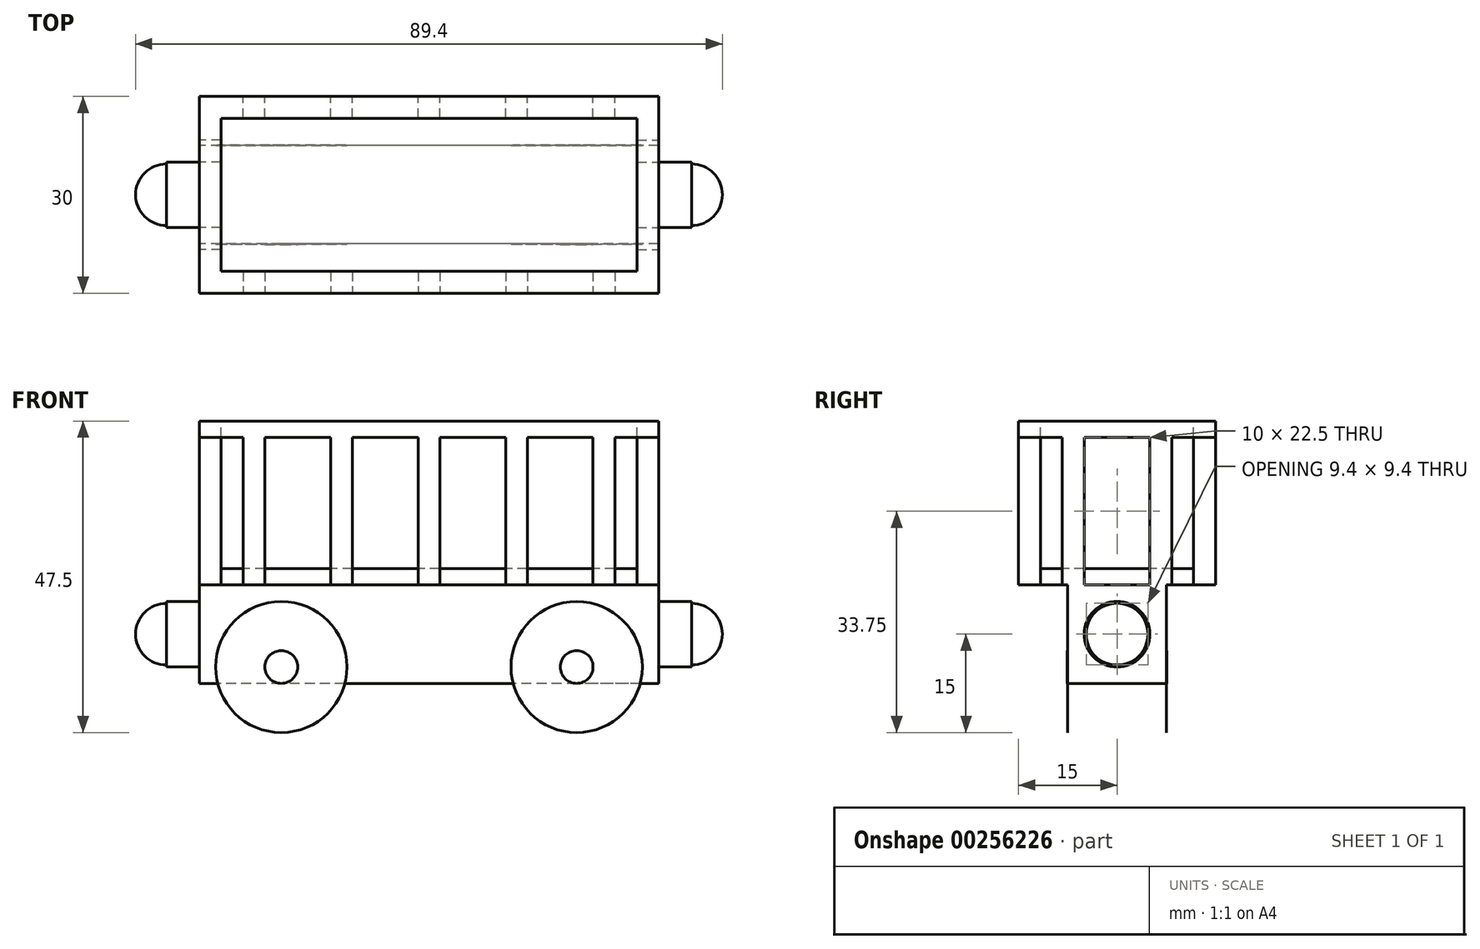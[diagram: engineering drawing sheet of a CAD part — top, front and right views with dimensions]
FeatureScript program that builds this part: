
annotation { "Feature Type Name" : "Feature", "Feature Type Description" : "" }
export const myFeature = defineFeature(function(context is Context, id is Id, definition is map)
    precondition{}
    {
        {
            var Q0;
            Q0=qCreatedBy(makeId("Front.planeOp"),FACE);
            var sketch = newSketch(context, id + "F0", { "sketchPlane" : qUnion([Q0])});
            skLineSegment(sketch, "E0.bottom", {"start": v(35, 7.5) * mm, "end": v(-35, 7.5) * mm});
            skLineSegment(sketch, "E0.top", {"start": v(35, -7.5) * mm, "end": v(-35, -7.5) * mm});
            skLineSegment(sketch, "E0.left", {"start": v(35, 7.5) * mm, "end": v(35, -7.5) * mm});
            skLineSegment(sketch, "E0.right", {"start": v(-35, 7.5) * mm, "end": v(-35, -7.5) * mm});
            skPoint(sketch, "E0.middle", {"position": v(0, 0) * mm});
            skSolve(sketch);
        }
        {
            var Q0;
            Q0=makeQuery(id+"F0.imprint","IMPRINT",FACE,{"disambiguationData":[TD([[makeQuery(id+"F0.imprint","IMPRINT",EDGE,{"derivedFrom":sQuery(id+"F0.wireOp",EDGE,"E0.bottom")}),1.0]])]});
            extrude(context, id + "F1", {"entities" : qUnion([Q0]), "flatOperationType" : FlatOperationType.REMOVE, "endBound" : BoundingType.SYMMETRIC, "offsetDistance" : 25.4 * mm, "depth" : 15 * mm, "domain" : OperationDomain.MODEL});
        }
        {
            var Q0;
            Q0=makeQuery(id+"F1.opExtrude","SWEPT_FACE",FACE,{"disambiguationData":[OSD([sQuery(id+"F0.wireOp",EDGE,"E0.left")])]});
            var sketch = newSketch(context, id + "F2", { "sketchPlane" : qUnion([Q0])});
            skCircle(sketch, "E1", {"center": v(0, 0) * mm, "radius": 5 * mm});
            skSolve(sketch);
        }
        {
            var Q0;
            Q0 = qSketchRegion(id + "F2", true);
            var Q1;
            Q1 = qSketchRegion(id + "F4", true);
            extrude(context, id + "F3", {"entities" : qUnion([Q0, Q1]), "operationType" : NewBodyOperationType.ADD, "flatOperationType" : FlatOperationType.REMOVE, "offsetDistance" : 25.4 * mm, "depth" : 5 * mm, "domain" : OperationDomain.MODEL});
        }
        {
            var Q0;
            Q0=makeQuery(id+"F3.opExtrude","CAP_FACE",FACE,{"disambiguationData":[OSD([sQuery(id+"F2.wireOp",EDGE,"E1")])],"isStart":false});
            var sketch = newSketch(context, id + "F4", { "sketchPlane" : qUnion([Q0])});
            skArc(sketch, "E2", {"start": v(0, -4.7) * mm, "mid": v(4.7, 0) * mm, "end": v(0, 4.7) * mm});
            skLineSegment(sketch, "E3", {"start": v(0, 4.7) * mm, "end": v(0, -4.7) * mm});
            skSolve(sketch);
        }
        {
            var Q0;
            Q0 = qSketchRegion(id + "F4", true);
            var Q1;
            Q1=sQuery(id+"F4.wireOp",EDGE,"E3");
            revolve(context, id + "F5", {"operationType" : NewBodyOperationType.ADD, "surfaceOperationType" : NewSurfaceOperationType.NEW, "entities" : qUnion([Q0]), "axis" : qUnion([Q1]), "revolveType" : RevolveType.FULL});
        }
        {
            var Q0;
            Q0=makeQuery(id+"F1.opExtrude","SWEPT_FACE",FACE,{"disambiguationData":[OSD([sQuery(id+"F0.wireOp",EDGE,"E0.right")])]});
            var sketch = newSketch(context, id + "F6", { "sketchPlane" : qUnion([Q0])});
            skCircle(sketch, "E4", {"center": v(0, 0) * mm, "radius": 5 * mm});
            skSolve(sketch);
        }
        {
            var Q0;
            Q0 = qSketchRegion(id + "F6", true);
            extrude(context, id + "F7", {"entities" : qUnion([Q0]), "operationType" : NewBodyOperationType.ADD, "depth" : 5 * mm});
        }
        {
            var Q0;
            Q0=makeQuery(id+"F7.opExtrude","CAP_FACE",FACE,{"disambiguationData":[OSD([sQuery(id+"F6.wireOp",EDGE,"E4")])],"isStart":false});
            var sketch = newSketch(context, id + "F8", { "sketchPlane" : qUnion([Q0])});
            skArc(sketch, "E5", {"start": v(0, -4.7) * mm, "mid": v(4.7, 0) * mm, "end": v(0, 4.7) * mm});
            skLineSegment(sketch, "E6", {"start": v(0, 4.7) * mm, "end": v(0, -4.7) * mm});
            skSolve(sketch);
        }
        {
            var Q0;
            Q0=makeQuery(id+"F8.imprint","IMPRINT",FACE,{"disambiguationData":[TD([[makeQuery(id+"F8.imprint","IMPRINT",EDGE,{"derivedFrom":sQuery(id+"F8.wireOp",EDGE,"E5")}),1.0]])]});
            var Q1;
            Q1=sQuery(id+"F8.wireOp",EDGE,"E6");
            revolve(context, id + "F9", {"operationType" : NewBodyOperationType.ADD, "entities" : qUnion([Q0]), "axis" : qUnion([Q1]), "revolveType" : RevolveType.FULL});
        }
        {
            var Q0;
            Q0=makeQuery(id+"F1.opExtrude","SWEPT_FACE",FACE,{"disambiguationData":[OSD([sQuery(id+"F0.wireOp",EDGE,"E0.bottom")])]});
            var sketch = newSketch(context, id + "F10", { "sketchPlane" : qUnion([Q0])});
            skLineSegment(sketch, "E7.bottom", {"start": v(35, 15) * mm, "end": v(-35, 15) * mm});
            skLineSegment(sketch, "E7.top", {"start": v(35, -15) * mm, "end": v(-35, -15) * mm});
            skLineSegment(sketch, "E7.left", {"start": v(35, 15) * mm, "end": v(35, -15) * mm});
            skLineSegment(sketch, "E7.right", {"start": v(-35, 15) * mm, "end": v(-35, -15) * mm});
            skPoint(sketch, "E7.middle", {"position": v(0, 0) * mm});
            skSolve(sketch);
        }
        {
            var Q0;
            Q0 = qSketchRegion(id + "F10", true);
            extrude(context, id + "F11", {"entities" : qUnion([Q0]), "operationType" : NewBodyOperationType.ADD, "flatOperationType" : FlatOperationType.REMOVE, "offsetDistance" : 25.4 * mm, "depth" : 25 * mm, "domain" : OperationDomain.MODEL});
        }
        {
            var Q0;
            Q0=makeQuery(id+"F11.opExtrude","CAP_FACE",FACE,{"disambiguationData":[OSD([sQuery(id+"F10.wireOp",EDGE,"E7.bottom"),sQuery(id+"F10.wireOp",EDGE,"E7.top"),sQuery(id+"F10.wireOp",EDGE,"E7.left"),sQuery(id+"F10.wireOp",EDGE,"E7.right")])],"isStart":false});
            var sketch = newSketch(context, id + "F12", { "sketchPlane" : qUnion([Q0])});
            skLineSegment(sketch, "E8.bottom", {"start": v(31.67, 11.67) * mm, "end": v(-31.67, 11.67) * mm});
            skLineSegment(sketch, "E8.top", {"start": v(31.67, -11.67) * mm, "end": v(-31.67, -11.67) * mm});
            skLineSegment(sketch, "E8.left", {"start": v(31.67, 11.67) * mm, "end": v(31.67, -11.67) * mm});
            skLineSegment(sketch, "E8.right", {"start": v(-31.67, 11.67) * mm, "end": v(-31.67, -11.67) * mm});
            skPoint(sketch, "E8.middle", {"position": v(0, 0) * mm});
            skSolve(sketch);
        }
        {
            var Q0;
            Q0 = qSketchRegion(id + "F12", true);
            extrude(context, id + "F13", {"entities" : qUnion([Q0]), "operationType" : NewBodyOperationType.REMOVE, "flatOperationType" : FlatOperationType.REMOVE, "oppositeDirection" : true, "offsetDistance" : 25.4 * mm, "depth" : 22.5 * mm, "domain" : OperationDomain.MODEL});
        }
        {
            var Q0;
            Q0=makeQuery(id+"F11.opExtrude","SWEPT_FACE",FACE,{"disambiguationData":[OSD([sQuery(id+"F10.wireOp",EDGE,"E7.top")])]});
            var sketch = newSketch(context, id + "F14", { "sketchPlane" : qUnion([Q0])});
            skLineSegment(sketch, "E9", {"start": v(0, 39.89) * mm, "end": v(0, -16.72) * mm, "construction": true});
            skLineSegment(sketch, "E10.bottom", {"start": v(11.67, 30) * mm, "end": v(1.67, 30) * mm});
            skLineSegment(sketch, "E10.top", {"start": v(11.67, 7.5) * mm, "end": v(1.67, 7.5) * mm});
            skLineSegment(sketch, "E10.left", {"start": v(11.67, 30) * mm, "end": v(11.67, 7.5) * mm});
            skLineSegment(sketch, "E10.right", {"start": v(1.67, 30) * mm, "end": v(1.67, 7.5) * mm});
            skPoint(sketch, "E10.middle", {"position": v(6.67, 18.75) * mm});
            skSolve(sketch);
        }
        {
            var Q0;
            Q0=makeQuery(id+"F14.imprint","IMPRINT",FACE,{"disambiguationData":[TD([[makeQuery(id+"F14.imprint","IMPRINT",EDGE,{"derivedFrom":sQuery(id+"F14.wireOp",EDGE,"E10.bottom")}),1.0]])]});
            extrude(context, id + "F15", {"entities" : qUnion([Q0]), "operationType" : NewBodyOperationType.REMOVE, "flatOperationType" : FlatOperationType.REMOVE, "oppositeDirection" : true, "offsetDistance" : 25.4 * mm, "depth" : 5 * mm, "domain" : OperationDomain.MODEL});
        }
        {
            var Q0;
            Q0=makeQuery(id+"F11.opExtrude","SWEPT_FACE",FACE,{"disambiguationData":[OSD([sQuery(id+"F10.wireOp",EDGE,"E7.bottom")])]});
            var sketch = newSketch(context, id + "F16", { "sketchPlane" : qUnion([Q0])});
            skLineSegment(sketch, "E11.0", {"start": v(-11.67, 30) * mm, "end": v(-11.67, 10) * mm});
            skPoint(sketch, "E12.0", {"position": v(-6.67, 30) * mm});
            skLineSegment(sketch, "E13.0", {"start": v(-11.67, 30) * mm, "end": v(-1.67, 30) * mm});
            skLineSegment(sketch, "E14.0", {"start": v(-1.67, 30) * mm, "end": v(-1.67, 10) * mm});
            skLineSegment(sketch, "E15.0", {"start": v(-11.67, 10) * mm, "end": v(-11.67, 7.5) * mm});
            skPoint(sketch, "E16.0", {"position": v(-1.67, 8.75) * mm});
            skPoint(sketch, "E17.0", {"position": v(-1.67, 7.5) * mm});
            skLineSegment(sketch, "E18.0", {"start": v(-1.67, 10) * mm, "end": v(-1.67, 7.5) * mm});
            skLineSegment(sketch, "E19.top", {"start": v(-11.67, 7.5) * mm, "end": v(-1.67, 7.5) * mm});
            skLineSegment(sketch, "E19.left", {"start": v(-11.67, 30) * mm, "end": v(-11.67, 7.5) * mm});
            skLineSegment(sketch, "E19.right", {"start": v(-1.67, 30) * mm, "end": v(-1.67, 7.5) * mm});
            skSolve(sketch);
        }
        {
            var Q0;
            Q0 = qSketchRegion(id + "F16", true);
            extrude(context, id + "F17", {"entities" : qUnion([Q0]), "operationType" : NewBodyOperationType.REMOVE, "flatOperationType" : FlatOperationType.REMOVE, "oppositeDirection" : true, "offsetDistance" : 25.4 * mm, "depth" : 5 * mm, "domain" : OperationDomain.MODEL});
        }
        {
            var Q0;
            Q0=makeQuery(id+"F11.opExtrude","SWEPT_FACE",FACE,{"disambiguationData":[OSD([sQuery(id+"F10.wireOp",EDGE,"E7.top")])]});
            var sketch = newSketch(context, id + "F18", { "sketchPlane" : qUnion([Q0])});
            skLineSegment(sketch, "E20.bottom", {"start": v(25, 30) * mm, "end": v(15, 30) * mm});
            skLineSegment(sketch, "E20.top", {"start": v(25, 7.5) * mm, "end": v(15, 7.5) * mm});
            skLineSegment(sketch, "E20.left", {"start": v(25, 30) * mm, "end": v(25, 7.5) * mm});
            skLineSegment(sketch, "E20.right", {"start": v(15, 30) * mm, "end": v(15, 7.5) * mm});
            skPoint(sketch, "E20.middle", {"position": v(20, 18.75) * mm});
            skSolve(sketch);
        }
        {
            var Q0;
            Q0=makeQuery(id+"F18.imprint","IMPRINT",FACE,{"disambiguationData":[TD([[makeQuery(id+"F18.imprint","IMPRINT",EDGE,{"derivedFrom":sQuery(id+"F18.wireOp",EDGE,"E20.bottom")}),1.0]])]});
            extrude(context, id + "F19", {"entities" : qUnion([Q0]), "operationType" : NewBodyOperationType.REMOVE, "oppositeDirection" : true, "depth" : 5 * mm});
        }
        {
            var Q0;
            Q0=makeQuery(id+"F11.opExtrude","SWEPT_FACE",FACE,{"disambiguationData":[OSD([sQuery(id+"F10.wireOp",EDGE,"E7.bottom")])]});
            var sketch = newSketch(context, id + "F20", { "sketchPlane" : qUnion([Q0])});
            skLineSegment(sketch, "E21.0", {"start": v(-25, 30) * mm, "end": v(-25, 10) * mm});
            skLineSegment(sketch, "E22.0", {"start": v(-25, 30) * mm, "end": v(-15, 30) * mm});
            skLineSegment(sketch, "E23.0", {"start": v(-15, 30) * mm, "end": v(-15, 10) * mm});
            skLineSegment(sketch, "E24.0", {"start": v(-25, 10) * mm, "end": v(-25, 7.5) * mm});
            skLineSegment(sketch, "E25.0", {"start": v(-15, 10) * mm, "end": v(-15, 7.5) * mm});
            skLineSegment(sketch, "E26", {"start": v(-25, 7.5) * mm, "end": v(-15, 7.5) * mm});
            skSolve(sketch);
        }
        {
            var Q0;
            Q0 = qSketchRegion(id + "F20", true);
            extrude(context, id + "F21", {"entities" : qUnion([Q0]), "operationType" : NewBodyOperationType.REMOVE, "oppositeDirection" : true, "depth" : 5 * mm});
        }
        {
            var Q0;
            Q0=makeQuery(id+"F11.opExtrude","SWEPT_FACE",FACE,{"disambiguationData":[OSD([sQuery(id+"F10.wireOp",EDGE,"E7.top")])]});
            var sketch = newSketch(context, id + "F22", { "sketchPlane" : qUnion([Q0])});
            skLineSegment(sketch, "E27.bottom", {"start": v(-1.67, 30) * mm, "end": v(-11.67, 30) * mm});
            skLineSegment(sketch, "E27.top", {"start": v(-1.67, 7.5) * mm, "end": v(-11.67, 7.5) * mm});
            skLineSegment(sketch, "E27.left", {"start": v(-1.67, 30) * mm, "end": v(-1.67, 7.5) * mm});
            skLineSegment(sketch, "E27.right", {"start": v(-11.67, 30) * mm, "end": v(-11.67, 7.5) * mm});
            skPoint(sketch, "E27.middle", {"position": v(-6.67, 18.75) * mm});
            skSolve(sketch);
        }
        {
            var Q0;
            Q0 = qSketchRegion(id + "F22", true);
            extrude(context, id + "F23", {"entities" : qUnion([Q0]), "operationType" : NewBodyOperationType.REMOVE, "oppositeDirection" : true, "depth" : 5 * mm});
        }
        {
            var Q0;
            Q0=makeQuery(id+"F11.opExtrude","SWEPT_FACE",FACE,{"disambiguationData":[OSD([sQuery(id+"F10.wireOp",EDGE,"E7.top")])]});
            var sketch = newSketch(context, id + "F24", { "sketchPlane" : qUnion([Q0])});
            skLineSegment(sketch, "E28.bottom", {"start": v(-15, 30) * mm, "end": v(-25, 30) * mm});
            skLineSegment(sketch, "E28.top", {"start": v(-15, 7.5) * mm, "end": v(-25, 7.5) * mm});
            skLineSegment(sketch, "E28.left", {"start": v(-15, 30) * mm, "end": v(-15, 7.5) * mm});
            skLineSegment(sketch, "E28.right", {"start": v(-25, 30) * mm, "end": v(-25, 7.5) * mm});
            skPoint(sketch, "E28.middle", {"position": v(-20, 18.75) * mm});
            skSolve(sketch);
        }
        {
            var Q0;
            Q0 = qSketchRegion(id + "F24", true);
            extrude(context, id + "F25", {"entities" : qUnion([Q0]), "operationType" : NewBodyOperationType.REMOVE, "flatOperationType" : FlatOperationType.REMOVE, "oppositeDirection" : true, "offsetDistance" : 25.4 * mm, "depth" : 5 * mm, "domain" : OperationDomain.MODEL});
        }
        {
            var Q0;
            Q0=makeQuery(id+"F11.opExtrude","SWEPT_FACE",FACE,{"disambiguationData":[OSD([sQuery(id+"F10.wireOp",EDGE,"E7.bottom")])]});
            var sketch = newSketch(context, id + "F26", { "sketchPlane" : qUnion([Q0])});
            skLineSegment(sketch, "E29.0", {"start": v(1.67, 30) * mm, "end": v(11.67, 30) * mm});
            skLineSegment(sketch, "E30.0", {"start": v(1.67, 30) * mm, "end": v(1.67, 10) * mm});
            skLineSegment(sketch, "E31.0", {"start": v(11.67, 30) * mm, "end": v(11.67, 10) * mm});
            skLineSegment(sketch, "E32.0", {"start": v(11.67, 10) * mm, "end": v(11.67, 7.5) * mm});
            skLineSegment(sketch, "E33.0", {"start": v(1.67, 10) * mm, "end": v(1.67, 7.5) * mm});
            skPoint(sketch, "E34.0", {"position": v(15, 8.75) * mm});
            skLineSegment(sketch, "E35.0", {"start": v(15, 30) * mm, "end": v(15, 10) * mm});
            skLineSegment(sketch, "E36.0", {"start": v(15, 30) * mm, "end": v(25, 30) * mm});
            skLineSegment(sketch, "E37.0", {"start": v(25, 30) * mm, "end": v(25, 10) * mm});
            skLineSegment(sketch, "E38.0", {"start": v(25, 10) * mm, "end": v(25, 7.5) * mm});
            skPoint(sketch, "E39.0", {"position": v(15, 7.5) * mm});
            skLineSegment(sketch, "E40.0", {"start": v(15, 10) * mm, "end": v(15, 7.5) * mm});
            skLineSegment(sketch, "E41", {"start": v(1.67, 7.5) * mm, "end": v(11.67, 7.5) * mm});
            skLineSegment(sketch, "E42", {"start": v(15, 7.5) * mm, "end": v(25, 7.5) * mm});
            skSolve(sketch);
        }
        {
            var Q0;
            Q0 = qSketchRegion(id + "F26", true);
            extrude(context, id + "F27", {"entities" : qUnion([Q0]), "operationType" : NewBodyOperationType.REMOVE, "oppositeDirection" : true, "depth" : 5 * mm});
        }
        {
            var Q0;
            Q0=makeQuery(id+"F11.boolean.opBoolean","MERGE",FACE,{"derivedFrom":[makeQuery(id+"F1.opExtrude","SWEPT_FACE",FACE,{"disambiguationData":[OSD([sQuery(id+"F0.wireOp",EDGE,"E0.left")])]}),makeQuery(id+"F11.opExtrude","SWEPT_FACE",FACE,{"disambiguationData":[OSD([sQuery(id+"F10.wireOp",EDGE,"E7.left")])]})]});
            var sketch = newSketch(context, id + "F28", { "sketchPlane" : qUnion([Q0])});
            skLineSegment(sketch, "E43.bottom", {"start": v(5, 30) * mm, "end": v(-5, 30) * mm});
            skLineSegment(sketch, "E43.top", {"start": v(5, 7.5) * mm, "end": v(-5, 7.5) * mm});
            skLineSegment(sketch, "E43.left", {"start": v(5, 30) * mm, "end": v(5, 7.5) * mm});
            skLineSegment(sketch, "E43.right", {"start": v(-5, 30) * mm, "end": v(-5, 7.5) * mm});
            skPoint(sketch, "E43.middle", {"position": v(0, 18.75) * mm});
            skSolve(sketch);
        }
        {
            var Q0;
            Q0 = qSketchRegion(id + "F28", true);
            extrude(context, id + "F29", {"entities" : qUnion([Q0]), "operationType" : NewBodyOperationType.REMOVE, "oppositeDirection" : true, "depth" : 5 * mm});
        }
        {
            var Q0;
            Q0=makeQuery(id+"F11.boolean.opBoolean","MERGE",FACE,{"derivedFrom":[makeQuery(id+"F1.opExtrude","SWEPT_FACE",FACE,{"disambiguationData":[OSD([sQuery(id+"F0.wireOp",EDGE,"E0.right")])]}),makeQuery(id+"F11.opExtrude","SWEPT_FACE",FACE,{"disambiguationData":[OSD([sQuery(id+"F10.wireOp",EDGE,"E7.right")])]})]});
            var sketch = newSketch(context, id + "F30", { "sketchPlane" : qUnion([Q0])});
            skLineSegment(sketch, "E44.0", {"start": v(-5, 30) * mm, "end": v(5, 30) * mm});
            skLineSegment(sketch, "E45.0", {"start": v(-5, 30) * mm, "end": v(-5, 10) * mm});
            skLineSegment(sketch, "E46.0", {"start": v(-5, 10) * mm, "end": v(-5, 7.5) * mm});
            skLineSegment(sketch, "E47.0", {"start": v(-5, 7.5) * mm, "end": v(5, 7.5) * mm});
            skLineSegment(sketch, "E48.0", {"start": v(5, 30) * mm, "end": v(5, 10) * mm});
            skLineSegment(sketch, "E49.0", {"start": v(5, 10) * mm, "end": v(5, 7.5) * mm});
            skSolve(sketch);
        }
        {
            var Q0;
            Q0 = qSketchRegion(id + "F30", true);
            extrude(context, id + "F31", {"entities" : qUnion([Q0]), "operationType" : NewBodyOperationType.REMOVE, "oppositeDirection" : true, "depth" : 5 * mm});
        }
        {
            var Q0;
            Q0=makeQuery(id+"F11.opExtrude","SWEPT_FACE",FACE,{"disambiguationData":[OSD([sQuery(id+"F10.wireOp",EDGE,"E7.bottom")])]});
            var sketch = newSketch(context, id + "F32", { "sketchPlane" : qUnion([Q0])});
            skLineSegment(sketch, "E50.bottom", {"start": v(28.33, 30) * mm, "end": v(38.33, 30) * mm});
            skLineSegment(sketch, "E50.top", {"start": v(28.33, 7.5) * mm, "end": v(38.33, 7.5) * mm});
            skLineSegment(sketch, "E50.left", {"start": v(28.33, 30) * mm, "end": v(28.33, 7.5) * mm});
            skLineSegment(sketch, "E50.right", {"start": v(38.33, 30) * mm, "end": v(38.33, 7.5) * mm});
            skSolve(sketch);
        }
        {
            var Q0;
            Q0 = qSketchRegion(id + "F32", true);
            extrude(context, id + "F33", {"entities" : qUnion([Q0]), "operationType" : NewBodyOperationType.REMOVE, "flatOperationType" : FlatOperationType.REMOVE, "oppositeDirection" : true, "offsetDistance" : 25.4 * mm, "depth" : 5 * mm, "domain" : OperationDomain.MODEL});
        }
        {
            var Q0;
            Q0=makeQuery(id+"F11.boolean.opBoolean","MERGE",FACE,{"derivedFrom":[makeQuery(id+"F1.opExtrude","SWEPT_FACE",FACE,{"disambiguationData":[OSD([sQuery(id+"F0.wireOp",EDGE,"E0.right")])]}),makeQuery(id+"F11.opExtrude","SWEPT_FACE",FACE,{"disambiguationData":[OSD([sQuery(id+"F10.wireOp",EDGE,"E7.right")])]})]});
            var sketch = newSketch(context, id + "F34", { "sketchPlane" : qUnion([Q0])});
            skPoint(sketch, "E51.oppositeSnap0", {"position": v(-8.75, 7.5) * mm});
            skLineSegment(sketch, "E51.bottom", {"start": v(-10, 30) * mm, "end": v(-8.33, 30) * mm});
            skLineSegment(sketch, "E51.top", {"start": v(-10, 7.5) * mm, "end": v(-8.33, 7.5) * mm});
            skLineSegment(sketch, "E51.left", {"start": v(-10, 30) * mm, "end": v(-10, 7.5) * mm});
            skLineSegment(sketch, "E51.right", {"start": v(-8.33, 30) * mm, "end": v(-8.33, 7.5) * mm});
            skSolve(sketch);
        }
        {
            var Q0;
            Q0 = qSketchRegion(id + "F34", true);
            extrude(context, id + "F35", {"entities" : qUnion([Q0]), "operationType" : NewBodyOperationType.REMOVE, "oppositeDirection" : true, "depth" : 5 * mm});
        }
        {
            var Q0;
            Q0=makeQuery(id+"F11.opExtrude","SWEPT_FACE",FACE,{"disambiguationData":[OSD([sQuery(id+"F10.wireOp",EDGE,"E7.top")])]});
            var sketch = newSketch(context, id + "F36", { "sketchPlane" : qUnion([Q0])});
            skLineSegment(sketch, "E52.bottom", {"start": v(-28.33, 30) * mm, "end": v(-38.33, 30) * mm});
            skLineSegment(sketch, "E52.top", {"start": v(-28.33, 7.5) * mm, "end": v(-38.33, 7.5) * mm});
            skLineSegment(sketch, "E52.left", {"start": v(-28.33, 30) * mm, "end": v(-28.33, 7.5) * mm});
            skLineSegment(sketch, "E52.right", {"start": v(-38.33, 30) * mm, "end": v(-38.33, 7.5) * mm});
            skSolve(sketch);
        }
        {
            var Q0;
            Q0 = qSketchRegion(id + "F36", true);
            extrude(context, id + "F37", {"entities" : qUnion([Q0]), "operationType" : NewBodyOperationType.REMOVE, "oppositeDirection" : true, "depth" : 5 * mm});
        }
        {
            var Q0;
            Q0=makeQuery(id+"F11.boolean.opBoolean","MERGE",FACE,{"derivedFrom":[makeQuery(id+"F1.opExtrude","SWEPT_FACE",FACE,{"disambiguationData":[OSD([sQuery(id+"F0.wireOp",EDGE,"E0.right")])]}),makeQuery(id+"F11.opExtrude","SWEPT_FACE",FACE,{"disambiguationData":[OSD([sQuery(id+"F10.wireOp",EDGE,"E7.right")])]})]});
            var sketch = newSketch(context, id + "F38", { "sketchPlane" : qUnion([Q0])});
            skLineSegment(sketch, "E53.bottom", {"start": v(10, 30) * mm, "end": v(8.33, 30) * mm});
            skLineSegment(sketch, "E53.top", {"start": v(10, 7.5) * mm, "end": v(8.33, 7.5) * mm});
            skLineSegment(sketch, "E53.left", {"start": v(10, 30) * mm, "end": v(10, 7.5) * mm});
            skLineSegment(sketch, "E53.right", {"start": v(8.33, 30) * mm, "end": v(8.33, 7.5) * mm});
            skSolve(sketch);
        }
        {
            var Q0;
            Q0 = qSketchRegion(id + "F38", true);
            extrude(context, id + "F39", {"entities" : qUnion([Q0]), "operationType" : NewBodyOperationType.REMOVE, "flatOperationType" : FlatOperationType.REMOVE, "oppositeDirection" : true, "offsetDistance" : 25.4 * mm, "depth" : 5 * mm, "domain" : OperationDomain.MODEL});
        }
        {
            var Q0;
            Q0=makeQuery(id+"F11.opExtrude","SWEPT_FACE",FACE,{"disambiguationData":[OSD([sQuery(id+"F10.wireOp",EDGE,"E7.bottom")])]});
            var sketch = newSketch(context, id + "F40", { "sketchPlane" : qUnion([Q0])});
            skLineSegment(sketch, "E54.bottom", {"start": v(-28.33, 30) * mm, "end": v(-36.23, 30) * mm});
            skLineSegment(sketch, "E54.top", {"start": v(-28.33, 7.5) * mm, "end": v(-36.23, 7.5) * mm});
            skLineSegment(sketch, "E54.left", {"start": v(-28.33, 30) * mm, "end": v(-28.33, 7.5) * mm});
            skLineSegment(sketch, "E54.right", {"start": v(-36.23, 30) * mm, "end": v(-36.23, 7.5) * mm});
            skSolve(sketch);
        }
        {
            var Q0;
            Q0 = qSketchRegion(id + "F40", true);
            extrude(context, id + "F41", {"entities" : qUnion([Q0]), "operationType" : NewBodyOperationType.REMOVE, "flatOperationType" : FlatOperationType.REMOVE, "oppositeDirection" : true, "offsetDistance" : 25.4 * mm, "depth" : 5 * mm, "domain" : OperationDomain.MODEL});
        }
        {
            var Q0;
            Q0=makeQuery(id+"F11.boolean.opBoolean","MERGE",FACE,{"derivedFrom":[makeQuery(id+"F1.opExtrude","SWEPT_FACE",FACE,{"disambiguationData":[OSD([sQuery(id+"F0.wireOp",EDGE,"E0.left")])]}),makeQuery(id+"F11.opExtrude","SWEPT_FACE",FACE,{"disambiguationData":[OSD([sQuery(id+"F10.wireOp",EDGE,"E7.left")])]})]});
            var sketch = newSketch(context, id + "F42", { "sketchPlane" : qUnion([Q0])});
            skLineSegment(sketch, "E55.bottom", {"start": v(8.33, 30) * mm, "end": v(10, 30) * mm});
            skLineSegment(sketch, "E55.top", {"start": v(8.33, 7.5) * mm, "end": v(10, 7.5) * mm});
            skLineSegment(sketch, "E55.left", {"start": v(8.33, 30) * mm, "end": v(8.33, 7.5) * mm});
            skLineSegment(sketch, "E55.right", {"start": v(10, 30) * mm, "end": v(10, 7.5) * mm});
            skSolve(sketch);
        }
        {
            var Q0;
            Q0 = qSketchRegion(id + "F42", true);
            extrude(context, id + "F43", {"entities" : qUnion([Q0]), "operationType" : NewBodyOperationType.REMOVE, "flatOperationType" : FlatOperationType.REMOVE, "oppositeDirection" : true, "offsetDistance" : 25.4 * mm, "depth" : 5 * mm, "domain" : OperationDomain.MODEL});
        }
        {
            var Q0;
            Q0=makeQuery(id+"F11.opExtrude","SWEPT_FACE",FACE,{"disambiguationData":[OSD([sQuery(id+"F10.wireOp",EDGE,"E7.top")])]});
            var sketch = newSketch(context, id + "F44", { "sketchPlane" : qUnion([Q0])});
            skLineSegment(sketch, "E56.bottom", {"start": v(28.33, 30) * mm, "end": v(36.5, 30) * mm});
            skLineSegment(sketch, "E56.top", {"start": v(28.33, 7.5) * mm, "end": v(36.5, 7.5) * mm});
            skLineSegment(sketch, "E56.left", {"start": v(28.33, 30) * mm, "end": v(28.33, 7.5) * mm});
            skLineSegment(sketch, "E56.right", {"start": v(36.5, 30) * mm, "end": v(36.5, 7.5) * mm});
            skSolve(sketch);
        }
        {
            var Q0;
            Q0 = qSketchRegion(id + "F44", true);
            extrude(context, id + "F45", {"entities" : qUnion([Q0]), "operationType" : NewBodyOperationType.REMOVE, "oppositeDirection" : true, "depth" : 5 * mm});
        }
        {
            var Q0;
            Q0=makeQuery(id+"F11.boolean.opBoolean","MERGE",FACE,{"derivedFrom":[makeQuery(id+"F1.opExtrude","SWEPT_FACE",FACE,{"disambiguationData":[OSD([sQuery(id+"F0.wireOp",EDGE,"E0.left")])]}),makeQuery(id+"F11.opExtrude","SWEPT_FACE",FACE,{"disambiguationData":[OSD([sQuery(id+"F10.wireOp",EDGE,"E7.left")])]})]});
            var sketch = newSketch(context, id + "F46", { "sketchPlane" : qUnion([Q0])});
            skLineSegment(sketch, "E57.bottom", {"start": v(-8.33, 30) * mm, "end": v(-10.68, 30) * mm});
            skLineSegment(sketch, "E57.top", {"start": v(-8.33, 7.5) * mm, "end": v(-10.68, 7.5) * mm});
            skLineSegment(sketch, "E57.left", {"start": v(-8.33, 30) * mm, "end": v(-8.33, 7.5) * mm});
            skLineSegment(sketch, "E57.right", {"start": v(-10.68, 30) * mm, "end": v(-10.68, 7.5) * mm});
            skSolve(sketch);
        }
        {
            var Q0;
            Q0 = qSketchRegion(id + "F46", true);
            extrude(context, id + "F47", {"entities" : qUnion([Q0]), "operationType" : NewBodyOperationType.REMOVE, "flatOperationType" : FlatOperationType.REMOVE, "oppositeDirection" : true, "offsetDistance" : 25.4 * mm, "depth" : 5 * mm, "domain" : OperationDomain.MODEL});
        }
        {
            var Q0;
            Q0=makeQuery(id+"F21.boolean.opBoolean","COPY",FACE,{"derivedFrom":makeQuery(id+"F21.opExtrude","CAP_FACE",FACE,{"disambiguationData":[OSD([sQuery(id+"F20.wireOp",EDGE,"E21.0"),sQuery(id+"F20.wireOp",EDGE,"E22.0"),sQuery(id+"F20.wireOp",EDGE,"E23.0"),sQuery(id+"F20.wireOp",EDGE,"E24.0"),sQuery(id+"F20.wireOp",EDGE,"E25.0"),sQuery(id+"F20.wireOp",EDGE,"E26")])],"isStart":false})});
            var sketch = newSketch(context, id + "F48", { "sketchPlane" : qUnion([Q0])});
            skLineSegment(sketch, "E58.bottom", {"start": v(-15, 7.5) * mm, "end": v(-25, 7.5) * mm});
            skLineSegment(sketch, "E58.top", {"start": v(-15, 10) * mm, "end": v(-25, 10) * mm});
            skLineSegment(sketch, "E58.left", {"start": v(-15, 7.5) * mm, "end": v(-15, 10) * mm});
            skLineSegment(sketch, "E58.right", {"start": v(-25, 7.5) * mm, "end": v(-25, 10) * mm});
            skSolve(sketch);
        }
        {
            var Q0;
            Q0 = qSketchRegion(id + "F48", true);
            var Q1;
            Q1 = qSketchRegion(id + "F58", true);
            extrude(context, id + "F49", {"entities" : qUnion([Q0, Q1]), "operationType" : NewBodyOperationType.ADD, "flatOperationType" : FlatOperationType.REMOVE, "offsetDistance" : 25.4 * mm, "depth" : 1.67 * mm, "domain" : OperationDomain.MODEL});
        }
        {
            var Q0;
            Q0=makeQuery(id+"F17.boolean.opBoolean","COPY",FACE,{"derivedFrom":makeQuery(id+"F17.opExtrude","CAP_FACE",FACE,{"disambiguationData":[OSD([sQuery(id+"F16.wireOp",EDGE,"E13.0"),sQuery(id+"F16.wireOp",EDGE,"E19.top"),sQuery(id+"F16.wireOp",EDGE,"E19.left"),sQuery(id+"F16.wireOp",EDGE,"E19.right")])],"isStart":false})});
            var sketch = newSketch(context, id + "F50", { "sketchPlane" : qUnion([Q0])});
            skLineSegment(sketch, "E59.bottom", {"start": v(-11.67, 10) * mm, "end": v(-1.67, 10) * mm});
            skLineSegment(sketch, "E59.top", {"start": v(-11.67, 7.5) * mm, "end": v(-1.67, 7.5) * mm});
            skLineSegment(sketch, "E59.left", {"start": v(-11.67, 10) * mm, "end": v(-11.67, 7.5) * mm});
            skLineSegment(sketch, "E59.right", {"start": v(-1.67, 10) * mm, "end": v(-1.67, 7.5) * mm});
            skSolve(sketch);
        }
        {
            var Q0;
            Q0 = qSketchRegion(id + "F50", true);
            extrude(context, id + "F51", {"entities" : qUnion([Q0]), "operationType" : NewBodyOperationType.ADD, "depth" : 1.67 * mm});
        }
        {
            var Q0;
            Q0=makeQuery(id+"F27.boolean.opBoolean","COPY",FACE,{"derivedFrom":makeQuery(id+"F27.opExtrude","CAP_FACE",FACE,{"disambiguationData":[OSD([sQuery(id+"F26.wireOp",EDGE,"E29.0"),sQuery(id+"F26.wireOp",EDGE,"E30.0"),sQuery(id+"F26.wireOp",EDGE,"E31.0"),sQuery(id+"F26.wireOp",EDGE,"E32.0"),sQuery(id+"F26.wireOp",EDGE,"E33.0"),sQuery(id+"F26.wireOp",EDGE,"E41")])],"isStart":false})});
            var sketch = newSketch(context, id + "F52", { "sketchPlane" : qUnion([Q0])});
            skLineSegment(sketch, "E60.bottom", {"start": v(1.67, 10) * mm, "end": v(11.67, 10) * mm});
            skLineSegment(sketch, "E60.top", {"start": v(1.67, 7.5) * mm, "end": v(11.67, 7.5) * mm});
            skLineSegment(sketch, "E60.left", {"start": v(1.67, 10) * mm, "end": v(1.67, 7.5) * mm});
            skLineSegment(sketch, "E60.right", {"start": v(11.67, 10) * mm, "end": v(11.67, 7.5) * mm});
            skSolve(sketch);
        }
        {
            var Q0;
            Q0 = qSketchRegion(id + "F52", true);
            extrude(context, id + "F53", {"entities" : qUnion([Q0]), "operationType" : NewBodyOperationType.ADD, "depth" : 1.67 * mm});
        }
        {
            var Q0;
            Q0=makeQuery(id+"F27.boolean.opBoolean","COPY",FACE,{"derivedFrom":makeQuery(id+"F27.opExtrude","CAP_FACE",FACE,{"disambiguationData":[OSD([sQuery(id+"F26.wireOp",EDGE,"E35.0"),sQuery(id+"F26.wireOp",EDGE,"E36.0"),sQuery(id+"F26.wireOp",EDGE,"E37.0"),sQuery(id+"F26.wireOp",EDGE,"E38.0"),sQuery(id+"F26.wireOp",EDGE,"E40.0"),sQuery(id+"F26.wireOp",EDGE,"E42")])],"isStart":false})});
            var sketch = newSketch(context, id + "F54", { "sketchPlane" : qUnion([Q0])});
            skLineSegment(sketch, "E61.bottom", {"start": v(15, 10) * mm, "end": v(25, 10) * mm});
            skLineSegment(sketch, "E61.top", {"start": v(15, 7.5) * mm, "end": v(25, 7.5) * mm});
            skLineSegment(sketch, "E61.left", {"start": v(15, 10) * mm, "end": v(15, 7.5) * mm});
            skLineSegment(sketch, "E61.right", {"start": v(25, 10) * mm, "end": v(25, 7.5) * mm});
            skSolve(sketch);
        }
        {
            var Q0;
            Q0 = qSketchRegion(id + "F54", true);
            extrude(context, id + "F55", {"entities" : qUnion([Q0]), "operationType" : NewBodyOperationType.ADD, "depth" : 1.67 * mm});
        }
        {
            var Q0;
            Q0=makeQuery(id+"F33.boolean.opBoolean","COPY",FACE,{"derivedFrom":makeQuery(id+"F33.opExtrude","CAP_FACE",FACE,{"disambiguationData":[OSD([sQuery(id+"F32.wireOp",EDGE,"E50.bottom"),sQuery(id+"F32.wireOp",EDGE,"E50.top"),sQuery(id+"F32.wireOp",EDGE,"E50.left"),sQuery(id+"F32.wireOp",EDGE,"E50.right")])],"isStart":false})});
            var sketch = newSketch(context, id + "F56", { "sketchPlane" : qUnion([Q0])});
            skLineSegment(sketch, "E62.bottom", {"start": v(28.33, 10) * mm, "end": v(30, 10) * mm});
            skLineSegment(sketch, "E62.top", {"start": v(28.33, 7.5) * mm, "end": v(30, 7.5) * mm});
            skLineSegment(sketch, "E62.left", {"start": v(28.33, 10) * mm, "end": v(28.33, 7.5) * mm});
            skLineSegment(sketch, "E62.right", {"start": v(30, 10) * mm, "end": v(30, 7.5) * mm});
            skSolve(sketch);
        }
        {
            var Q0;
            Q0 = qSketchRegion(id + "F56", true);
            extrude(context, id + "F57", {"entities" : qUnion([Q0]), "operationType" : NewBodyOperationType.ADD, "depth" : 1.67 * mm});
        }
        {
            var Q0;
            Q0=makeQuery(id+"F57.boolean.opBoolean","MERGE",FACE,{"derivedFrom":[makeQuery(id+"F35.boolean.opBoolean","COPY",FACE,{"derivedFrom":makeQuery(id+"F35.opExtrude","CAP_FACE",FACE,{"disambiguationData":[OSD([sQuery(id+"F34.wireOp",EDGE,"E51.bottom"),sQuery(id+"F34.wireOp",EDGE,"E51.top"),sQuery(id+"F34.wireOp",EDGE,"E51.left"),sQuery(id+"F34.wireOp",EDGE,"E51.right")])],"isStart":false})}),makeQuery(id+"F57.opExtrude","SWEPT_FACE",FACE,{"disambiguationData":[OSD([sQuery(id+"F56.wireOp",EDGE,"E62.right")])]})]});
            var sketch = newSketch(context, id + "F58", { "sketchPlane" : qUnion([Q0])});
            skLineSegment(sketch, "E63.bottom", {"start": v(-11.67, 10) * mm, "end": v(-8.33, 10) * mm});
            skLineSegment(sketch, "E63.top", {"start": v(-11.67, 7.5) * mm, "end": v(-8.33, 7.5) * mm});
            skLineSegment(sketch, "E63.left", {"start": v(-11.67, 10) * mm, "end": v(-11.67, 7.5) * mm});
            skLineSegment(sketch, "E63.right", {"start": v(-8.33, 10) * mm, "end": v(-8.33, 7.5) * mm});
            skSolve(sketch);
        }
        {
            var Q0;
            Q0 = qSketchRegion(id + "F58", true);
            extrude(context, id + "F59", {"entities" : qUnion([Q0]), "operationType" : NewBodyOperationType.ADD, "flatOperationType" : FlatOperationType.REMOVE, "offsetDistance" : 25.4 * mm, "depth" : 1.67 * mm, "domain" : OperationDomain.MODEL});
        }
        {
            var Q0;
            Q0=makeQuery(id+"F31.boolean.opBoolean","COPY",FACE,{"derivedFrom":makeQuery(id+"F31.opExtrude","CAP_FACE",FACE,{"disambiguationData":[OSD([sQuery(id+"F30.wireOp",EDGE,"E44.0"),sQuery(id+"F30.wireOp",EDGE,"E45.0"),sQuery(id+"F30.wireOp",EDGE,"E46.0"),sQuery(id+"F30.wireOp",EDGE,"E47.0"),sQuery(id+"F30.wireOp",EDGE,"E48.0"),sQuery(id+"F30.wireOp",EDGE,"E49.0")])],"isStart":false})});
            var sketch = newSketch(context, id + "F60", { "sketchPlane" : qUnion([Q0])});
            skLineSegment(sketch, "E64.bottom", {"start": v(-5, 10) * mm, "end": v(5, 10) * mm});
            skLineSegment(sketch, "E64.top", {"start": v(-5, 7.5) * mm, "end": v(5, 7.5) * mm});
            skLineSegment(sketch, "E64.left", {"start": v(-5, 10) * mm, "end": v(-5, 7.5) * mm});
            skLineSegment(sketch, "E64.right", {"start": v(5, 10) * mm, "end": v(5, 7.5) * mm});
            skSolve(sketch);
        }
        {
            var Q0;
            Q0 = qSketchRegion(id + "F60", true);
            extrude(context, id + "F61", {"entities" : qUnion([Q0]), "operationType" : NewBodyOperationType.ADD, "depth" : 1.67 * mm});
        }
        {
            var Q0;
            Q0=makeQuery(id+"F39.boolean.opBoolean","COPY",FACE,{"derivedFrom":makeQuery(id+"F39.opExtrude","CAP_FACE",FACE,{"disambiguationData":[OSD([sQuery(id+"F38.wireOp",EDGE,"E53.bottom"),sQuery(id+"F38.wireOp",EDGE,"E53.top"),sQuery(id+"F38.wireOp",EDGE,"E53.left"),sQuery(id+"F38.wireOp",EDGE,"E53.right")])],"isStart":false})});
            var sketch = newSketch(context, id + "F62", { "sketchPlane" : qUnion([Q0])});
            skLineSegment(sketch, "E65.bottom", {"start": v(8.33, 10) * mm, "end": v(10, 10) * mm});
            skLineSegment(sketch, "E65.top", {"start": v(8.33, 7.5) * mm, "end": v(10, 7.5) * mm});
            skLineSegment(sketch, "E65.left", {"start": v(8.33, 10) * mm, "end": v(8.33, 7.5) * mm});
            skLineSegment(sketch, "E65.right", {"start": v(10, 10) * mm, "end": v(10, 7.5) * mm});
            skSolve(sketch);
        }
        {
            var Q0;
            Q0 = qSketchRegion(id + "F62", true);
            extrude(context, id + "F63", {"entities" : qUnion([Q0]), "operationType" : NewBodyOperationType.ADD, "depth" : 1.67 * mm});
        }
        {
            var Q0;
            Q0=makeQuery(id+"F63.boolean.opBoolean","MERGE",FACE,{"derivedFrom":[makeQuery(id+"F37.boolean.opBoolean","COPY",FACE,{"derivedFrom":makeQuery(id+"F37.opExtrude","CAP_FACE",FACE,{"disambiguationData":[OSD([sQuery(id+"F36.wireOp",EDGE,"E52.bottom"),sQuery(id+"F36.wireOp",EDGE,"E52.top"),sQuery(id+"F36.wireOp",EDGE,"E52.left"),sQuery(id+"F36.wireOp",EDGE,"E52.right")])],"isStart":false})}),makeQuery(id+"F63.opExtrude","SWEPT_FACE",FACE,{"disambiguationData":[OSD([sQuery(id+"F62.wireOp",EDGE,"E65.right")])]})]});
            var sketch = newSketch(context, id + "F64", { "sketchPlane" : qUnion([Q0])});
            skLineSegment(sketch, "E66.bottom", {"start": v(-31.67, 10) * mm, "end": v(-28.33, 10) * mm});
            skLineSegment(sketch, "E66.top", {"start": v(-31.67, 7.5) * mm, "end": v(-28.33, 7.5) * mm});
            skLineSegment(sketch, "E66.left", {"start": v(-31.67, 10) * mm, "end": v(-31.67, 7.5) * mm});
            skLineSegment(sketch, "E66.right", {"start": v(-28.33, 10) * mm, "end": v(-28.33, 7.5) * mm});
            skSolve(sketch);
        }
        {
            var Q0;
            Q0 = qSketchRegion(id + "F64", true);
            extrude(context, id + "F65", {"entities" : qUnion([Q0]), "operationType" : NewBodyOperationType.ADD, "depth" : 1.67 * mm});
        }
        {
            var Q0;
            Q0=makeQuery(id+"F25.boolean.opBoolean","COPY",FACE,{"derivedFrom":makeQuery(id+"F25.opExtrude","CAP_FACE",FACE,{"disambiguationData":[OSD([sQuery(id+"F24.wireOp",EDGE,"E28.bottom"),sQuery(id+"F24.wireOp",EDGE,"E28.top"),sQuery(id+"F24.wireOp",EDGE,"E28.left"),sQuery(id+"F24.wireOp",EDGE,"E28.right")])],"isStart":false})});
            var sketch = newSketch(context, id + "F66", { "sketchPlane" : qUnion([Q0])});
            skLineSegment(sketch, "E67.bottom", {"start": v(-25, 10) * mm, "end": v(-15, 10) * mm});
            skLineSegment(sketch, "E67.top", {"start": v(-25, 7.5) * mm, "end": v(-15, 7.5) * mm});
            skLineSegment(sketch, "E67.left", {"start": v(-25, 10) * mm, "end": v(-25, 7.5) * mm});
            skLineSegment(sketch, "E67.right", {"start": v(-15, 10) * mm, "end": v(-15, 7.5) * mm});
            skSolve(sketch);
        }
        {
            var Q0;
            Q0 = qSketchRegion(id + "F66", true);
            extrude(context, id + "F67", {"entities" : qUnion([Q0]), "operationType" : NewBodyOperationType.ADD, "flatOperationType" : FlatOperationType.REMOVE, "offsetDistance" : 25.4 * mm, "depth" : 1.67 * mm, "domain" : OperationDomain.MODEL});
        }
        {
            var Q0;
            Q0=makeQuery(id+"F23.boolean.opBoolean","COPY",FACE,{"derivedFrom":makeQuery(id+"F23.opExtrude","CAP_FACE",FACE,{"disambiguationData":[OSD([sQuery(id+"F22.wireOp",EDGE,"E27.bottom"),sQuery(id+"F22.wireOp",EDGE,"E27.top"),sQuery(id+"F22.wireOp",EDGE,"E27.left"),sQuery(id+"F22.wireOp",EDGE,"E27.right")])],"isStart":false})});
            var sketch = newSketch(context, id + "F68", { "sketchPlane" : qUnion([Q0])});
            skLineSegment(sketch, "E68.bottom", {"start": v(-11.67, 10) * mm, "end": v(-1.67, 10) * mm});
            skLineSegment(sketch, "E68.top", {"start": v(-11.67, 7.5) * mm, "end": v(-1.67, 7.5) * mm});
            skLineSegment(sketch, "E68.left", {"start": v(-11.67, 10) * mm, "end": v(-11.67, 7.5) * mm});
            skLineSegment(sketch, "E68.right", {"start": v(-1.67, 10) * mm, "end": v(-1.67, 7.5) * mm});
            skSolve(sketch);
        }
        {
            var Q0;
            Q0 = qSketchRegion(id + "F68", true);
            extrude(context, id + "F69", {"entities" : qUnion([Q0]), "operationType" : NewBodyOperationType.ADD, "depth" : 1.67 * mm});
        }
        {
            var Q0;
            Q0=makeQuery(id+"F15.boolean.opBoolean","COPY",FACE,{"derivedFrom":makeQuery(id+"F15.opExtrude","CAP_FACE",FACE,{"disambiguationData":[OSD([sQuery(id+"F14.wireOp",EDGE,"E10.bottom"),sQuery(id+"F14.wireOp",EDGE,"E10.top"),sQuery(id+"F14.wireOp",EDGE,"E10.left"),sQuery(id+"F14.wireOp",EDGE,"E10.right")])],"isStart":false})});
            var sketch = newSketch(context, id + "F70", { "sketchPlane" : qUnion([Q0])});
            skLineSegment(sketch, "E69.bottom", {"start": v(1.67, 10) * mm, "end": v(11.67, 10) * mm});
            skLineSegment(sketch, "E69.top", {"start": v(1.67, 7.5) * mm, "end": v(11.67, 7.5) * mm});
            skLineSegment(sketch, "E69.left", {"start": v(1.67, 10) * mm, "end": v(1.67, 7.5) * mm});
            skLineSegment(sketch, "E69.right", {"start": v(11.67, 10) * mm, "end": v(11.67, 7.5) * mm});
            skSolve(sketch);
        }
        {
            var Q0;
            Q0 = qSketchRegion(id + "F70", true);
            extrude(context, id + "F71", {"entities" : qUnion([Q0]), "operationType" : NewBodyOperationType.ADD, "depth" : 1.67 * mm});
        }
        {
            var Q0;
            Q0=makeQuery(id+"F19.boolean.opBoolean","COPY",FACE,{"derivedFrom":makeQuery(id+"F19.opExtrude","CAP_FACE",FACE,{"disambiguationData":[OSD([sQuery(id+"F18.wireOp",EDGE,"E20.bottom"),sQuery(id+"F18.wireOp",EDGE,"E20.top"),sQuery(id+"F18.wireOp",EDGE,"E20.left"),sQuery(id+"F18.wireOp",EDGE,"E20.right")])],"isStart":false})});
            var sketch = newSketch(context, id + "F72", { "sketchPlane" : qUnion([Q0])});
            skLineSegment(sketch, "E70.bottom", {"start": v(15, 10) * mm, "end": v(25, 10) * mm});
            skLineSegment(sketch, "E70.top", {"start": v(15, 7.5) * mm, "end": v(25, 7.5) * mm});
            skLineSegment(sketch, "E70.left", {"start": v(15, 10) * mm, "end": v(15, 7.5) * mm});
            skLineSegment(sketch, "E70.right", {"start": v(25, 10) * mm, "end": v(25, 7.5) * mm});
            skSolve(sketch);
        }
        {
            var Q0;
            Q0 = qSketchRegion(id + "F72", true);
            extrude(context, id + "F73", {"entities" : qUnion([Q0]), "operationType" : NewBodyOperationType.ADD, "depth" : 1.67 * mm});
        }
        {
            var Q0;
            Q0=makeQuery(id+"F45.boolean.opBoolean","COPY",FACE,{"derivedFrom":makeQuery(id+"F45.opExtrude","CAP_FACE",FACE,{"disambiguationData":[OSD([sQuery(id+"F44.wireOp",EDGE,"E56.bottom"),sQuery(id+"F44.wireOp",EDGE,"E56.top"),sQuery(id+"F44.wireOp",EDGE,"E56.left"),sQuery(id+"F44.wireOp",EDGE,"E56.right")])],"isStart":false})});
            var sketch = newSketch(context, id + "F74", { "sketchPlane" : qUnion([Q0])});
            skLineSegment(sketch, "E71.bottom", {"start": v(28.33, 10) * mm, "end": v(30, 10) * mm});
            skLineSegment(sketch, "E71.top", {"start": v(28.33, 7.5) * mm, "end": v(30, 7.5) * mm});
            skLineSegment(sketch, "E71.left", {"start": v(28.33, 10) * mm, "end": v(28.33, 7.5) * mm});
            skLineSegment(sketch, "E71.right", {"start": v(30, 10) * mm, "end": v(30, 7.5) * mm});
            skSolve(sketch);
        }
        {
            var Q0;
            Q0 = qSketchRegion(id + "F74", true);
            extrude(context, id + "F75", {"entities" : qUnion([Q0]), "operationType" : NewBodyOperationType.ADD, "flatOperationType" : FlatOperationType.REMOVE, "offsetDistance" : 25.4 * mm, "depth" : 1.67 * mm, "domain" : OperationDomain.MODEL});
        }
        {
            var Q0;
            Q0=makeQuery(id+"F75.boolean.opBoolean","MERGE",FACE,{"derivedFrom":[makeQuery(id+"F47.boolean.opBoolean","COPY",FACE,{"derivedFrom":makeQuery(id+"F47.opExtrude","CAP_FACE",FACE,{"disambiguationData":[OSD([sQuery(id+"F46.wireOp",EDGE,"E57.bottom"),sQuery(id+"F46.wireOp",EDGE,"E57.top"),sQuery(id+"F46.wireOp",EDGE,"E57.left"),sQuery(id+"F46.wireOp",EDGE,"E57.right")])],"isStart":false})}),makeQuery(id+"F75.opExtrude","SWEPT_FACE",FACE,{"disambiguationData":[OSD([sQuery(id+"F74.wireOp",EDGE,"E71.right")])]})]});
            var sketch = newSketch(context, id + "F76", { "sketchPlane" : qUnion([Q0])});
            skLineSegment(sketch, "E72.bottom", {"start": v(-11.67, 10) * mm, "end": v(-8.33, 10) * mm});
            skLineSegment(sketch, "E72.top", {"start": v(-11.67, 7.5) * mm, "end": v(-8.33, 7.5) * mm});
            skLineSegment(sketch, "E72.left", {"start": v(-11.67, 10) * mm, "end": v(-11.67, 7.5) * mm});
            skLineSegment(sketch, "E72.right", {"start": v(-8.33, 10) * mm, "end": v(-8.33, 7.5) * mm});
            skSolve(sketch);
        }
        {
            var Q0;
            Q0 = qSketchRegion(id + "F76", true);
            extrude(context, id + "F77", {"entities" : qUnion([Q0]), "operationType" : NewBodyOperationType.ADD, "depth" : 1.67 * mm});
        }
        {
            var Q0;
            Q0=makeQuery(id+"F29.boolean.opBoolean","COPY",FACE,{"derivedFrom":makeQuery(id+"F29.opExtrude","CAP_FACE",FACE,{"disambiguationData":[OSD([sQuery(id+"F28.wireOp",EDGE,"E43.bottom"),sQuery(id+"F28.wireOp",EDGE,"E43.top"),sQuery(id+"F28.wireOp",EDGE,"E43.left"),sQuery(id+"F28.wireOp",EDGE,"E43.right")])],"isStart":false})});
            var sketch = newSketch(context, id + "F78", { "sketchPlane" : qUnion([Q0])});
            skLineSegment(sketch, "E73.bottom", {"start": v(-5, 10) * mm, "end": v(5, 10) * mm});
            skLineSegment(sketch, "E73.top", {"start": v(-5, 7.5) * mm, "end": v(5, 7.5) * mm});
            skLineSegment(sketch, "E73.left", {"start": v(-5, 10) * mm, "end": v(-5, 7.5) * mm});
            skLineSegment(sketch, "E73.right", {"start": v(5, 10) * mm, "end": v(5, 7.5) * mm});
            skSolve(sketch);
        }
        {
            var Q0;
            Q0 = qSketchRegion(id + "F78", true);
            extrude(context, id + "F79", {"entities" : qUnion([Q0]), "operationType" : NewBodyOperationType.ADD, "flatOperationType" : FlatOperationType.REMOVE, "offsetDistance" : 25.4 * mm, "depth" : 1.67 * mm, "domain" : OperationDomain.MODEL});
        }
        {
            var Q0;
            Q0=makeQuery(id+"F43.boolean.opBoolean","COPY",FACE,{"derivedFrom":makeQuery(id+"F43.opExtrude","CAP_FACE",FACE,{"disambiguationData":[OSD([sQuery(id+"F42.wireOp",EDGE,"E55.bottom"),sQuery(id+"F42.wireOp",EDGE,"E55.top"),sQuery(id+"F42.wireOp",EDGE,"E55.left"),sQuery(id+"F42.wireOp",EDGE,"E55.right")])],"isStart":false})});
            var sketch = newSketch(context, id + "F80", { "sketchPlane" : qUnion([Q0])});
            skLineSegment(sketch, "E74.bottom", {"start": v(8.33, 10) * mm, "end": v(10, 10) * mm});
            skLineSegment(sketch, "E74.top", {"start": v(8.33, 7.5) * mm, "end": v(10, 7.5) * mm});
            skLineSegment(sketch, "E74.left", {"start": v(8.33, 10) * mm, "end": v(8.33, 7.5) * mm});
            skLineSegment(sketch, "E74.right", {"start": v(10, 10) * mm, "end": v(10, 7.5) * mm});
            skSolve(sketch);
        }
        {
            var Q0;
            Q0 = qSketchRegion(id + "F80", true);
            extrude(context, id + "F81", {"entities" : qUnion([Q0]), "operationType" : NewBodyOperationType.ADD, "depth" : 1.67 * mm});
        }
        {
            var Q0;
            Q0=makeQuery(id+"F81.boolean.opBoolean","MERGE",FACE,{"derivedFrom":[makeQuery(id+"F41.boolean.opBoolean","COPY",FACE,{"derivedFrom":makeQuery(id+"F41.opExtrude","CAP_FACE",FACE,{"disambiguationData":[OSD([sQuery(id+"F40.wireOp",EDGE,"E54.bottom"),sQuery(id+"F40.wireOp",EDGE,"E54.top"),sQuery(id+"F40.wireOp",EDGE,"E54.left"),sQuery(id+"F40.wireOp",EDGE,"E54.right")])],"isStart":false})}),makeQuery(id+"F81.opExtrude","SWEPT_FACE",FACE,{"disambiguationData":[OSD([sQuery(id+"F80.wireOp",EDGE,"E74.right")])]})]});
            var sketch = newSketch(context, id + "F82", { "sketchPlane" : qUnion([Q0])});
            skLineSegment(sketch, "E75.bottom", {"start": v(-31.67, 10) * mm, "end": v(-28.33, 10) * mm});
            skLineSegment(sketch, "E75.top", {"start": v(-31.67, 7.5) * mm, "end": v(-28.33, 7.5) * mm});
            skLineSegment(sketch, "E75.left", {"start": v(-31.67, 10) * mm, "end": v(-31.67, 7.5) * mm});
            skLineSegment(sketch, "E75.right", {"start": v(-28.33, 10) * mm, "end": v(-28.33, 7.5) * mm});
            skSolve(sketch);
        }
        {
            var Q0;
            Q0 = qSketchRegion(id + "F82", true);
            extrude(context, id + "F83", {"entities" : qUnion([Q0]), "operationType" : NewBodyOperationType.ADD, "flatOperationType" : FlatOperationType.REMOVE, "offsetDistance" : 25.4 * mm, "depth" : 1.67 * mm, "domain" : OperationDomain.MODEL});
        }
        {
            var Q0;
            Q0=makeQuery(id+"F1.opExtrude","CAP_FACE",FACE,{"disambiguationData":[OSD([sQuery(id+"F0.wireOp",EDGE,"E0.bottom"),sQuery(id+"F0.wireOp",EDGE,"E0.top"),sQuery(id+"F0.wireOp",EDGE,"E0.left"),sQuery(id+"F0.wireOp",EDGE,"E0.right")])],"isStart":true});
            var sketch = newSketch(context, id + "F84", { "sketchPlane" : qUnion([Q0])});
            skCircle(sketch, "E76", {"center": v(-22.5, -5) * mm, "radius": 2.5 * mm});
            skSolve(sketch);
        }
        {
            var Q0;
            Q0=makeQuery(id+"F84.imprint","IMPRINT",FACE,{"disambiguationData":[TD([[makeQuery(id+"F84.imprint","IMPRINT",EDGE,{"derivedFrom":sQuery(id+"F84.wireOp",EDGE,"E76")}),1.0]])]});
            extrude(context, id + "F85", {"entities" : qUnion([Q0]), "operationType" : NewBodyOperationType.ADD, "depth" : 1 / 40 * mm});
        }
        {
            var Q0;
            Q0=makeQuery(id+"F85.opExtrude","CAP_FACE",FACE,{"disambiguationData":[OSD([sQuery(id+"F84.wireOp",EDGE,"E76")])],"isStart":false});
            var sketch = newSketch(context, id + "F86", { "sketchPlane" : qUnion([Q0])});
            skCircle(sketch, "E77", {"center": v(-22.5, -5) * mm, "radius": 10 * mm});
            skSolve(sketch);
        }
        {
            var Q0;
            Q0 = qSketchRegion(id + "F86", true);
            extrude(context, id + "F87", {"entities" : qUnion([Q0]), "operationType" : NewBodyOperationType.ADD, "flatOperationType" : FlatOperationType.REMOVE, "offsetDistance" : 25.4 * mm, "depth" : 1 / 40 * mm, "domain" : OperationDomain.MODEL});
        }
        {
            var Q0;
            Q0=makeQuery(id+"F87.opExtrude","CAP_FACE",FACE,{"disambiguationData":[OSD([sQuery(id+"F86.wireOp",EDGE,"E77")])],"isStart":false});
            var sketch = newSketch(context, id + "F88", { "sketchPlane" : qUnion([Q0])});
            skCircle(sketch, "E78.0", {"center": v(-22.5, -5) * mm, "radius": 2.5 * mm});
            skSolve(sketch);
        }
        {
            var Q0;
            Q0=makeQuery(id+"F88.imprint","IMPRINT",FACE,{"disambiguationData":[TD([[makeQuery(id+"F88.imprint","IMPRINT",EDGE,{"derivedFrom":sQuery(id+"F88.wireOp",EDGE,"E78.0")}),1.0]])]});
            extrude(context, id + "F89", {"entities" : qUnion([Q0]), "operationType" : NewBodyOperationType.ADD, "depth" : 1 / 40 * mm});
        }
        {
            var Q0;
            Q0=makeQuery(id+"F1.opExtrude","CAP_FACE",FACE,{"disambiguationData":[OSD([sQuery(id+"F0.wireOp",EDGE,"E0.bottom"),sQuery(id+"F0.wireOp",EDGE,"E0.top"),sQuery(id+"F0.wireOp",EDGE,"E0.left"),sQuery(id+"F0.wireOp",EDGE,"E0.right")])],"isStart":true});
            var sketch = newSketch(context, id + "F90", { "sketchPlane" : qUnion([Q0])});
            skCircle(sketch, "E79", {"center": v(22.5, -5) * mm, "radius": 2.5 * mm});
            skSolve(sketch);
        }
        {
            var Q0;
            Q0 = qSketchRegion(id + "F90", true);
            extrude(context, id + "F91", {"entities" : qUnion([Q0]), "operationType" : NewBodyOperationType.ADD, "depth" : 1 / 40 * mm});
        }
        {
            var Q0;
            Q0=makeQuery(id+"F91.opExtrude","CAP_FACE",FACE,{"disambiguationData":[OSD([sQuery(id+"F90.wireOp",EDGE,"E79")])],"isStart":false});
            var sketch = newSketch(context, id + "F92", { "sketchPlane" : qUnion([Q0])});
            skCircle(sketch, "E80", {"center": v(22.5, -5) * mm, "radius": 10 * mm});
            skSolve(sketch);
        }
        {
            var Q0;
            Q0 = qSketchRegion(id + "F92", true);
            extrude(context, id + "F93", {"entities" : qUnion([Q0]), "operationType" : NewBodyOperationType.ADD, "depth" : 1 / 40 * mm});
        }
        {
            var Q0;
            Q0=makeQuery(id+"F93.opExtrude","CAP_FACE",FACE,{"disambiguationData":[OSD([sQuery(id+"F92.wireOp",EDGE,"E80")])],"isStart":false});
            var sketch = newSketch(context, id + "F94", { "sketchPlane" : qUnion([Q0])});
            skCircle(sketch, "E81.0", {"center": v(22.5, -5) * mm, "radius": 2.5 * mm});
            skSolve(sketch);
        }
        {
            var Q0;
            Q0 = qSketchRegion(id + "F94", true);
            extrude(context, id + "F95", {"entities" : qUnion([Q0]), "operationType" : NewBodyOperationType.ADD, "depth" : 1 / 40 * mm});
        }
        {
            var Q0;
            Q0=makeQuery(id+"F1.opExtrude","CAP_FACE",FACE,{"disambiguationData":[OSD([sQuery(id+"F0.wireOp",EDGE,"E0.bottom"),sQuery(id+"F0.wireOp",EDGE,"E0.top"),sQuery(id+"F0.wireOp",EDGE,"E0.left"),sQuery(id+"F0.wireOp",EDGE,"E0.right")])],"isStart":false});
            var sketch = newSketch(context, id + "F96", { "sketchPlane" : qUnion([Q0])});
            skCircle(sketch, "E82.0", {"center": v(-22.5, -5) * mm, "radius": 2.5 * mm});
            skSolve(sketch);
        }
        {
            var Q0;
            Q0 = qSketchRegion(id + "F96", true);
            extrude(context, id + "F97", {"entities" : qUnion([Q0]), "operationType" : NewBodyOperationType.ADD, "depth" : 1 / 40 * mm});
        }
        {
            var Q0;
            Q0=makeQuery(id+"F1.opExtrude","CAP_FACE",FACE,{"disambiguationData":[OSD([sQuery(id+"F0.wireOp",EDGE,"E0.bottom"),sQuery(id+"F0.wireOp",EDGE,"E0.top"),sQuery(id+"F0.wireOp",EDGE,"E0.left"),sQuery(id+"F0.wireOp",EDGE,"E0.right")])],"isStart":false});
            var sketch = newSketch(context, id + "F98", { "sketchPlane" : qUnion([Q0])});
            skCircle(sketch, "E83.0", {"center": v(22.5, -5) * mm, "radius": 2.5 * mm});
            skSolve(sketch);
        }
        {
            var Q0;
            Q0 = qSketchRegion(id + "F98", true);
            extrude(context, id + "F99", {"entities" : qUnion([Q0]), "operationType" : NewBodyOperationType.ADD, "depth" : 1 / 40 * mm});
        }
        {
            var Q0;
            Q0=makeQuery(id+"F97.opExtrude","CAP_FACE",FACE,{"disambiguationData":[OSD([sQuery(id+"F96.wireOp",EDGE,"E82.0")])],"isStart":false});
            var sketch = newSketch(context, id + "F100", { "sketchPlane" : qUnion([Q0])});
            skCircle(sketch, "E84.0", {"center": v(-22.5, -5) * mm, "radius": 10 * mm});
            skSolve(sketch);
        }
        {
            var Q0;
            Q0 = qSketchRegion(id + "F100", true);
            extrude(context, id + "F101", {"entities" : qUnion([Q0]), "operationType" : NewBodyOperationType.ADD, "depth" : 1 / 40 * mm});
        }
        {
            var Q0;
            Q0=makeQuery(id+"F99.opExtrude","CAP_FACE",FACE,{"disambiguationData":[OSD([sQuery(id+"F98.wireOp",EDGE,"E83.0")])],"isStart":false});
            var sketch = newSketch(context, id + "F102", { "sketchPlane" : qUnion([Q0])});
            skCircle(sketch, "E85.0", {"center": v(22.5, -5) * mm, "radius": 10 * mm});
            skSolve(sketch);
        }
        {
            var Q0;
            Q0 = qSketchRegion(id + "F102", true);
            extrude(context, id + "F103", {"entities" : qUnion([Q0]), "operationType" : NewBodyOperationType.ADD, "depth" : 1 / 40 * mm});
        }
        {
            var Q0;
            Q0=makeQuery(id+"F101.opExtrude","CAP_FACE",FACE,{"disambiguationData":[OSD([sQuery(id+"F100.wireOp",EDGE,"E84.0")])],"isStart":false});
            var sketch = newSketch(context, id + "F104", { "sketchPlane" : qUnion([Q0])});
            skCircle(sketch, "E86.0", {"center": v(-22.5, -5) * mm, "radius": 2.5 * mm});
            skSolve(sketch);
        }
        {
            var Q0;
            Q0 = qSketchRegion(id + "F104", true);
            extrude(context, id + "F105", {"entities" : qUnion([Q0]), "operationType" : NewBodyOperationType.ADD, "depth" : 1 / 40 * mm});
        }
        {
            var Q0;
            Q0=makeQuery(id+"F103.opExtrude","CAP_FACE",FACE,{"disambiguationData":[OSD([sQuery(id+"F102.wireOp",EDGE,"E85.0")])],"isStart":false});
            var sketch = newSketch(context, id + "F106", { "sketchPlane" : qUnion([Q0])});
            skCircle(sketch, "E87.0", {"center": v(22.5, -5) * mm, "radius": 2.5 * mm});
            skSolve(sketch);
        }
        {
            var Q0;
            Q0 = qSketchRegion(id + "F106", true);
            extrude(context, id + "F107", {"entities" : qUnion([Q0]), "operationType" : NewBodyOperationType.ADD, "depth" : 1 / 40 * mm});
        }
        {
            var Q0;
            Q0=makeQuery(id+"F87.opExtrude","CAP_EDGE",EDGE,{"disambiguationData":[OSD([sQuery(id+"F86.wireOp",EDGE,"E77")])],"isStart":false});
            fillet(context, id + "F108", {"entities" : qUnion([Q0]), "radius" : 1.27 * mm, "tangentPropagation" : true, "allowEdgeOverflow" : false});
        }
        {
            var Q0;
            Q0=makeQuery(id+"F93.opExtrude","CAP_EDGE",EDGE,{"disambiguationData":[OSD([sQuery(id+"F92.wireOp",EDGE,"E80")])],"isStart":false});
            fillet(context, id + "F109", {"entities" : qUnion([Q0]), "radius" : 1.27 * mm, "tangentPropagation" : true, "allowEdgeOverflow" : false});
        }
        {
            var Q0;
            Q0=makeQuery(id+"F101.opExtrude","CAP_EDGE",EDGE,{"disambiguationData":[OSD([sQuery(id+"F100.wireOp",EDGE,"E84.0")])],"isStart":false});
            fillet(context, id + "F110", {"entities" : qUnion([Q0]), "radius" : 1.27 * mm, "tangentPropagation" : true, "allowEdgeOverflow" : false});
        }
        {
            var Q0;
            Q0=makeQuery(id+"F103.opExtrude","CAP_EDGE",EDGE,{"disambiguationData":[OSD([sQuery(id+"F102.wireOp",EDGE,"E85.0")])],"isStart":false});
            fillet(context, id + "F111", {"entities" : qUnion([Q0]), "radius" : 1.27 * mm, "tangentPropagation" : true, "allowEdgeOverflow" : false});
        }
    });
